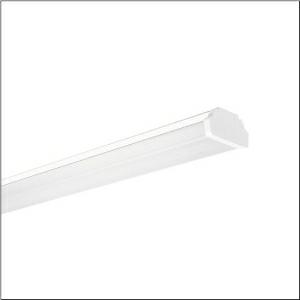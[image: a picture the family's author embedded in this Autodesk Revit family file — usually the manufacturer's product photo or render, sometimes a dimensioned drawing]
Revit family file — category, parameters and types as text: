
# Revit family: dus_31_gen_2_53bd812cv4a5d2_05be
name_source: partatom
category: Lighting Fixtures
units: mm (PartAtom-declared; Revit-internal decimal feet)

## family parameters
Cut with Voids When Loaded = No
Host = Face
Light Source = No
Part Type = Normal
Room Calculation Point = No
Round Connector Dimension = Use Diameter
Shared = No

## types (1)
- --- (1 x LED, 10570 lm, 54.8 W, 4000K)
    Apparent Load = 55 VA
    CIE Flux Codes = 47 80 95 93 100
    Color Rendering = 80
    Color Temperature = 4000K
    Default Elevation = 1800 mm
    Description = DUS 31 Gen.2, luminaire insert, of sheet steel, coil coated, white, length: 1.535mm, width: 81mm, height: 90mm, 5x system unit, system units: 307mm, LED rated luminous flux: 10.570lm, light colour: 840, SDCM (Standard Deviation of Colour Matching)MacAdam ≤ 3 SDCM (initial), control gear: ON/OFF Multilumen, CLOi, with plug, 3-pole, with phase selection, mains connection: 220..240V, AC, 50/60Hz, start of lifetime: 55W, end of service life: 65W, through-wiring accessed according to module size, primary optical cover: cover, of PMMA, light emission: direct distribution, primary light characteristic: symmetric, protection rating (complete): IP20, protection rating (LED compartment): IP50, insulation class (complete): insulation class I (protective earthing), certification: CE, ENEC, VDE, UKCA, impact resistance: IK03, permissible ambient temperature for indoor applications: -35..+40°C, corresponds to IFS (International Featured Standards) requirements for safety and quality in the food industry, reducing of maximum allowable ambient temperature of 5°C with ceiling mounting, packaging unit: 1 piece
    Height = 95 mm
    Lamp = 1 x LED
    Lamp Light Flux = 10570 lm
    Lamp Power = 54.8 W
    Lamp count = 1
    Length = 1535 mm
    Luminous efficacy = 193 lm/W
    Manufacturer = Siteco
    ModVariant = No
    Model = 53BD812CV4A5D2
    Mounting Place = Ceiling
    Mounting Type = Pendant
    Number of Poles = 1
    OnlyDefault = Yes
    Power Factor = 1
    Product Name = DUS 31 Gen.2
    Product group = luminaire insert | ceiling pendant
    ProductGroupID = 901
    Protection Class = Protection class I
    Protection Degree = IP 20
    RLX_Detail_Level = 1
    RLX_Emergency_Light_Flux = 0 lm
    RLX_Emergency_Type = 0
    RLX_Emergency_Type_DB = No
    RlxData = <blob elided: 29917 chars, md5=ba0f4f66>
    Socket = socket
    Standby Power = 0 W
    System Light Flux = 10570 lm
    System Power = 55 W
    Type Comments = factory setting: luminous flux: 100 % | (A | C | E) | 129 mA
    Type Image = l_1319596.jpg
    URL = http://relux.com
    VarID = @adj_040787
    Voltage = 0 V
    Weight = 0.00 kg
    Width = 81 mm

## geometry (parser evidence)
native form markers: Blend x4, Sweep x13
no freeform markers — native parametric forms only
